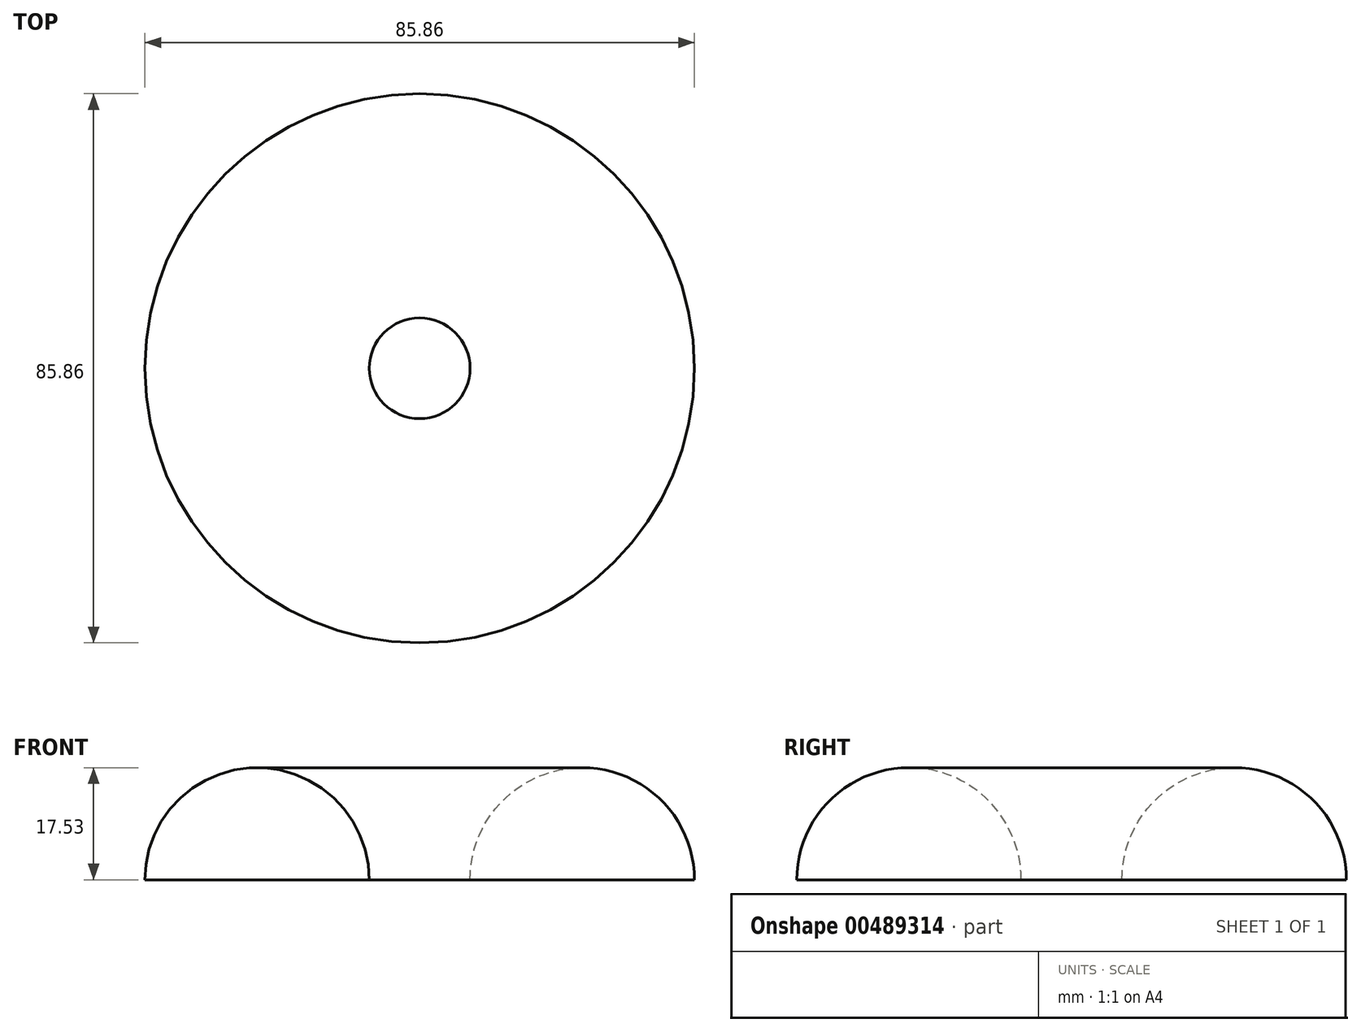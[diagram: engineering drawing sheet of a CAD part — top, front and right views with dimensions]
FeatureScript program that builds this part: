
annotation { "Feature Type Name" : "Feature", "Feature Type Description" : "" }
export const myFeature = defineFeature(function(context is Context, id is Id, definition is map)
    precondition{}
    {
        {
            var Q0;
            Q0=qCreatedBy(makeId("Front.planeOp"),FACE);
            var sketch = newSketch(context, id + "F0", { "sketchPlane" : qUnion([Q0])});
            skArc(sketch, "E0", {"start": v(42.93, 0) * mm, "mid": v(25.4, 17.53) * mm, "end": v(7.87, 0) * mm});
            skLineSegment(sketch, "E1", {"start": v(7.87, 0) * mm, "end": v(42.93, 0) * mm});
            skSolve(sketch);
        }
        {
            var Q0;
            Q0=qCreatedBy(makeId("Front.planeOp"),FACE);
            var sketch = newSketch(context, id + "F1", { "sketchPlane" : qUnion([Q0])});
            skLineSegment(sketch, "E2", {"start": v(0, 0) * mm, "end": v(0, 35.47) * mm});
            skSolve(sketch);
        }
        {
            var Q0;
            Q0 = qSketchRegion(id + "F0", true);
            var Q1;
            Q1=sQuery(id+"F1.wireOp",EDGE,"E2");
            revolve(context, id + "F2", {"entities" : qUnion([Q0]), "axis" : qUnion([Q1]), "revolveType" : RevolveType.FULL});
        }
    });
